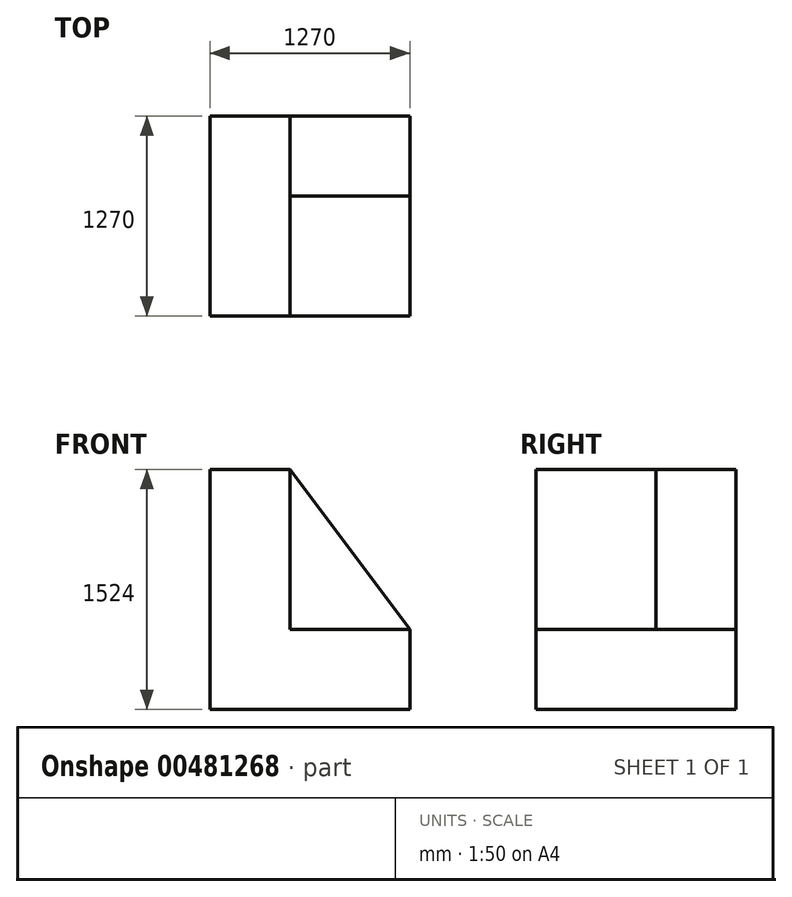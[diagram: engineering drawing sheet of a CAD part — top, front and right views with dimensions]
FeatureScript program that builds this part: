
annotation { "Feature Type Name" : "Feature", "Feature Type Description" : "" }
export const myFeature = defineFeature(function(context is Context, id is Id, definition is map)
    precondition{}
    {
        {
            var Q0;
            Q0=qCreatedBy(makeId("Front.planeOp"),FACE);
            var sketch = newSketch(context, id + "F0", { "sketchPlane" : qUnion([Q0])});
            skLineSegment(sketch, "E0", {"start": v(0, 0) * mm, "end": v(0, 1524) * mm});
            skLineSegment(sketch, "E1", {"start": v(0, 1524) * mm, "end": v(508, 1524) * mm});
            skLineSegment(sketch, "E2", {"start": v(508, 1524) * mm, "end": v(508, 508) * mm});
            skLineSegment(sketch, "E3", {"start": v(508, 508) * mm, "end": v(1270, 508) * mm});
            skLineSegment(sketch, "E4", {"start": v(1270, 508) * mm, "end": v(1270, 0) * mm});
            skLineSegment(sketch, "E5", {"start": v(0, 0) * mm, "end": v(1270, 0) * mm});
            skSolve(sketch);
        }
        {
            var Q0;
            Q0=makeQuery(id+"F0.imprint","IMPRINT",FACE,{"disambiguationData":[TD([[makeQuery(id+"F0.imprint","IMPRINT",EDGE,{"derivedFrom":sQuery(id+"F0.wireOp",EDGE,"E0")}),-1.0]])]});
            extrude(context, id + "F1", {"entities" : qUnion([Q0]), "depth" : 1270 * mm});
        }
        {
            var Q0;
            Q0=makeQuery(id+"F1.opExtrude","CAP_FACE",FACE,{"disambiguationData":[OSD([sQuery(id+"F0.wireOp",EDGE,"E0"),sQuery(id+"F0.wireOp",EDGE,"E1"),sQuery(id+"F0.wireOp",EDGE,"E2"),sQuery(id+"F0.wireOp",EDGE,"E3"),sQuery(id+"F0.wireOp",EDGE,"E4"),sQuery(id+"F0.wireOp",EDGE,"E5")])],"isStart":true});
            var sketch = newSketch(context, id + "F2", { "sketchPlane" : qUnion([Q0])});
            skLineSegment(sketch, "E6", {"start": v(-508, 1524) * mm, "end": v(-1270, 508) * mm});
            skLineSegment(sketch, "E7", {"start": v(-1237.56, 508) * mm, "end": v(-508, 508) * mm});
            skLineSegment(sketch, "E8", {"start": v(-508, 508) * mm, "end": v(-508, 1524) * mm});
            skSolve(sketch);
        }
        {
            var Q0;
            {var subQ0=sQuery(id+"F2.wireOp",EDGE,"E6");Q0=makeQuery(id+"F2.imprint","IMPRINT",FACE,{"disambiguationData":[TD([[makeQuery(id+"F2.imprint","IMPRINT",EDGE,{"derivedFrom":subQ0}),1.0]])]});}
            extrude(context, id + "F3", {"entities" : qUnion([Q0]), "operationType" : NewBodyOperationType.ADD, "oppositeDirection" : true, "depth" : 508 * mm});
        }
    });
